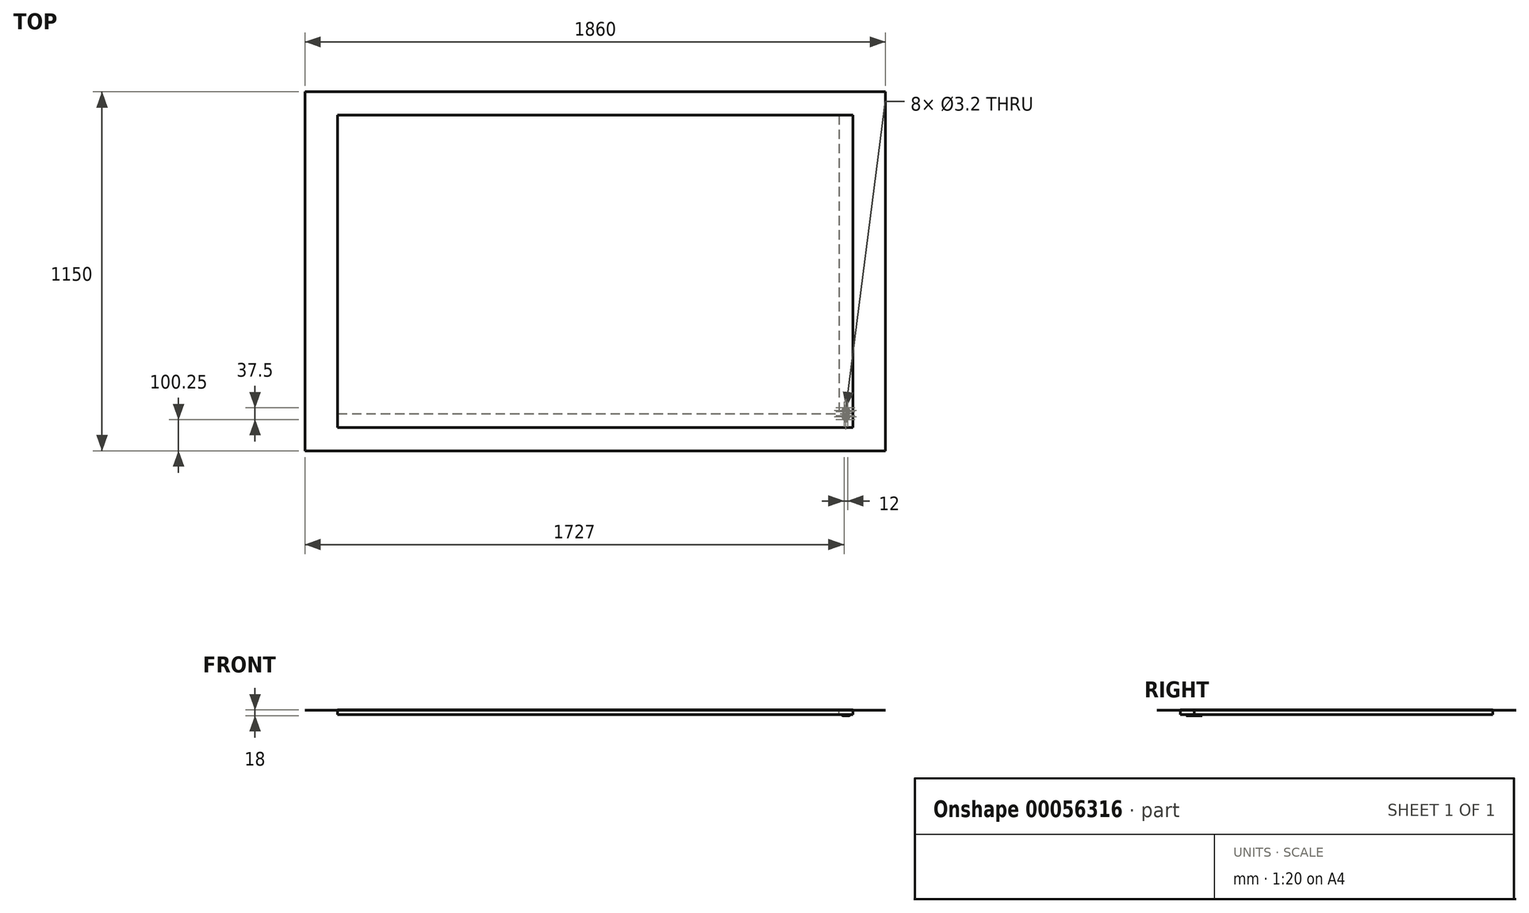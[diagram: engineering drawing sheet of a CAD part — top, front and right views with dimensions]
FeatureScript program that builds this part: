
annotation { "Feature Type Name" : "Feature", "Feature Type Description" : "" }
export const myFeature = defineFeature(function(context is Context, id is Id, definition is map)
    precondition{}
    {
        {
            var Q0;
            Q0=qCreatedBy(makeId("Top.planeOp"),FACE);
            var sketch = newSketch(context, id + "F0", { "sketchPlane" : qUnion([Q0])});
            skLineSegment(sketch, "E0.bottom", {"start": v(825, 500) * mm, "end": v(-825, 500) * mm});
            skLineSegment(sketch, "E0.top", {"start": v(825, -500) * mm, "end": v(-825, -500) * mm});
            skLineSegment(sketch, "E0.left", {"start": v(825, 500) * mm, "end": v(825, -500) * mm});
            skLineSegment(sketch, "E0.right", {"start": v(-825, 500) * mm, "end": v(-825, -500) * mm});
            skPoint(sketch, "E0.middle", {"position": v(0, 0) * mm});
            skSolve(sketch);
        }
        {
            var Q0;
            Q0 = qSketchRegion(id + "F0", true);
            extrude(context, id + "F1", {"entities" : qUnion([Q0]), "depth" : 1 * mm, "offsetDistance" : 25 * mm});
        }
        {
            var Q0;
            Q0=makeQuery(id+"F1.opExtrude","CAP_FACE",FACE,{"disambiguationData":[OSD([sQuery(id+"F0.wireOp",EDGE,"E0.bottom"),sQuery(id+"F0.wireOp",EDGE,"E0.top"),sQuery(id+"F0.wireOp",EDGE,"E0.left"),sQuery(id+"F0.wireOp",EDGE,"E0.right")])],"isStart":true});
            var sketch = newSketch(context, id + "F2", { "sketchPlane" : qUnion([Q0])});
            skLineSegment(sketch, "E1.bottom", {"start": v(930, -575) * mm, "end": v(-930, -575) * mm});
            skLineSegment(sketch, "E1.top", {"start": v(930, 575) * mm, "end": v(-930, 575) * mm});
            skLineSegment(sketch, "E1.left", {"start": v(930, -575) * mm, "end": v(930, 575) * mm});
            skLineSegment(sketch, "E1.right", {"start": v(-930, -575) * mm, "end": v(-930, 575) * mm});
            skPoint(sketch, "E1.middle", {"position": v(0, 0) * mm});
            skSolve(sketch);
        }
        {
            var Q0;
            Q0 = qSketchRegion(id + "F2", true);
            extrude(context, id + "F3", {"entities" : qUnion([Q0]), "depth" : 0.1 * mm, "offsetDistance" : 25 * mm});
        }
        {
            var Q0;
            Q0=makeQuery(id+"F1.opExtrude","CAP_FACE",FACE,{"disambiguationData":[OSD([sQuery(id+"F0.wireOp",EDGE,"E0.bottom"),sQuery(id+"F0.wireOp",EDGE,"E0.top"),sQuery(id+"F0.wireOp",EDGE,"E0.left"),sQuery(id+"F0.wireOp",EDGE,"E0.right")])],"isStart":true});
            var sketch = newSketch(context, id + "F4", { "sketchPlane" : qUnion([Q0])});
            skLineSegment(sketch, "E2.bottom", {"start": v(-825, 500) * mm, "end": v(825, 500) * mm});
            skLineSegment(sketch, "E2.top", {"start": v(-825, 456) * mm, "end": v(825, 456) * mm});
            skLineSegment(sketch, "E2.left", {"start": v(-825, 500) * mm, "end": v(-825, 456) * mm});
            skLineSegment(sketch, "E2.right", {"start": v(825, 500) * mm, "end": v(825, 456) * mm});
            skSolve(sketch);
        }
        {
            var Q0;
            Q0 = qSketchRegion(id + "F4", true);
            extrude(context, id + "F5", {"entities" : qUnion([Q0]), "depth" : 14 * mm, "offsetDistance" : 25 * mm});
        }
        {
            var Q0;
            Q0=makeQuery(id+"F1.opExtrude","CAP_FACE",FACE,{"disambiguationData":[OSD([sQuery(id+"F0.wireOp",EDGE,"E0.bottom"),sQuery(id+"F0.wireOp",EDGE,"E0.top"),sQuery(id+"F0.wireOp",EDGE,"E0.left"),sQuery(id+"F0.wireOp",EDGE,"E0.right")])],"isStart":true});
            var sketch = newSketch(context, id + "F6", { "sketchPlane" : qUnion([Q0])});
            skLineSegment(sketch, "E3.bottom", {"start": v(825, -500) * mm, "end": v(781, -500) * mm});
            skLineSegment(sketch, "E3.top", {"start": v(825, 456) * mm, "end": v(781, 456) * mm});
            skLineSegment(sketch, "E3.left", {"start": v(825, -500) * mm, "end": v(825, 456) * mm});
            skLineSegment(sketch, "E3.right", {"start": v(781, -500) * mm, "end": v(781, 456) * mm});
            skSolve(sketch);
        }
        {
            var Q0;
            Q0 = qSketchRegion(id + "F6", true);
            extrude(context, id + "F7", {"entities" : qUnion([Q0]), "depth" : 14 * mm, "offsetDistance" : 25 * mm});
        }
        {
            var Q0;
            Q0=makeQuery(id+"F5.opExtrude","CAP_FACE",FACE,{"disambiguationData":[OSD([sQuery(id+"F4.wireOp",EDGE,"E2.bottom"),sQuery(id+"F4.wireOp",EDGE,"E2.top"),sQuery(id+"F4.wireOp",EDGE,"E2.left"),sQuery(id+"F4.wireOp",EDGE,"E2.right")])],"isStart":false});
            var sketch = newSketch(context, id + "F8", { "sketchPlane" : qUnion([Q0])});
            skLineSegment(sketch, "E4.bottom", {"start": v(798, 456) * mm, "end": v(808, 456) * mm, "construction": true});
            skLineSegment(sketch, "E4.top", {"start": v(801, 431) * mm, "end": v(805, 431) * mm});
            skLineSegment(sketch, "E4.left", {"start": v(798, 456) * mm, "end": v(798, 434) * mm});
            skLineSegment(sketch, "E4.right", {"start": v(808, 456) * mm, "end": v(808, 434) * mm});
            skLineSegment(sketch, "E5", {"start": v(808, 431) * mm, "end": v(825, 431) * mm, "construction": true});
            skLineSegment(sketch, "E6", {"start": v(798, 431) * mm, "end": v(781, 431) * mm, "construction": true});
            skLineSegment(sketch, "E7", {"start": v(803, 431) * mm, "end": v(803, 456) * mm, "construction": true});
            skCircle(sketch, "E8", {"center": v(803, 437.25) * mm, "radius": 1.6 * mm});
            skLineSegment(sketch, "E9", {"start": v(808, 443.5) * mm, "end": v(798, 443.5) * mm, "construction": true});
            skCircle(sketch, "E10.MirrorC", {"center": v(803, 449.75) * mm, "radius": 1.6 * mm});
            skLineSegment(sketch, "E11", {"start": v(803, 443.5) * mm, "end": v(803, 431) * mm, "construction": true});
            skCircle(sketch, "E12.MirrorC", {"center": v(803, 474.75) * mm, "radius": 1.6 * mm});
            skCircle(sketch, "E13.MirrorC", {"center": v(803, 462.25) * mm, "radius": 1.6 * mm});
            skLineSegment(sketch, "E14.MirrorCS", {"start": v(801, 481) * mm, "end": v(805, 481) * mm});
            skLineSegment(sketch, "E15.MirrorCS", {"start": v(808, 456) * mm, "end": v(808, 478) * mm});
            skLineSegment(sketch, "E16.MirrorCS", {"start": v(798, 456) * mm, "end": v(798, 478) * mm});
            skPoint(sketch, "E17.visualSharp", {"position": v(798, 481) * mm});
            skArc(sketch, "E17.filletArc", {"start": v(801, 481) * mm, "mid": v(798.88, 480.12) * mm, "end": v(798, 478) * mm});
            skPoint(sketch, "E18.visualSharp", {"position": v(808, 481) * mm});
            skArc(sketch, "E18.filletArc", {"start": v(808, 478) * mm, "mid": v(807.12, 480.12) * mm, "end": v(805, 481) * mm});
            skPoint(sketch, "E19.visualSharp", {"position": v(808, 431) * mm});
            skArc(sketch, "E19.filletArc", {"start": v(805, 431) * mm, "mid": v(807.12, 431.88) * mm, "end": v(808, 434) * mm});
            skPoint(sketch, "E20.visualSharp", {"position": v(798, 431) * mm});
            skArc(sketch, "E20.filletArc", {"start": v(798, 434) * mm, "mid": v(798.88, 431.88) * mm, "end": v(801, 431) * mm});
            skSolve(sketch);
        }
        {
            var Q0;
            Q0 = qSketchRegion(id + "F8", true);
            extrude(context, id + "F9", {"entities" : qUnion([Q0]), "depth" : 3 * mm, "offsetDistance" : 25 * mm});
        }
        {
            var Q0;
            Q0=makeQuery(id+"F5.opExtrude","CAP_FACE",FACE,{"disambiguationData":[OSD([sQuery(id+"F4.wireOp",EDGE,"E2.bottom"),sQuery(id+"F4.wireOp",EDGE,"E2.top"),sQuery(id+"F4.wireOp",EDGE,"E2.left"),sQuery(id+"F4.wireOp",EDGE,"E2.right")])],"isStart":false});
            var sketch = newSketch(context, id + "F10", { "sketchPlane" : qUnion([Q0])});
            skLineSegment(sketch, "E21.bottom", {"start": v(794, 451) * mm, "end": v(798, 451) * mm});
            skLineSegment(sketch, "E21.top", {"start": v(794, 441) * mm, "end": v(812, 441) * mm});
            skLineSegment(sketch, "E21.left", {"start": v(791, 448) * mm, "end": v(791, 444) * mm});
            skLineSegment(sketch, "E21.right", {"start": v(815, 448) * mm, "end": v(815, 444) * mm});
            skLineSegment(sketch, "E22", {"start": v(791, 446) * mm, "end": v(781, 446) * mm, "construction": true});
            skLineSegment(sketch, "E23", {"start": v(815, 446) * mm, "end": v(825, 446) * mm, "construction": true});
            skLineSegment(sketch, "E24", {"start": v(791, 446) * mm, "end": v(803, 446) * mm, "construction": true});
            skPoint(sketch, "E24.endSnap0", {"position": v(803, 451) * mm});
            skLineSegment(sketch, "E25", {"start": v(803, 446) * mm, "end": v(803, 451) * mm, "construction": true});
            skCircle(sketch, "E26", {"center": v(797, 446) * mm, "radius": 1.6 * mm});
            skCircle(sketch, "E27.MirrorC", {"center": v(809, 446) * mm, "radius": 1.6 * mm});
            skLineSegment(sketch, "E28.top", {"start": v(798, 456) * mm, "end": v(808, 456) * mm});
            skLineSegment(sketch, "E28.left", {"start": v(798, 451) * mm, "end": v(798, 456) * mm});
            skLineSegment(sketch, "E28.right", {"start": v(808, 451) * mm, "end": v(808, 456) * mm});
            skLineSegment(sketch, "E29", {"start": v(803, 456) * mm, "end": v(803, 451) * mm, "construction": true});
            skLineSegment(sketch, "E30.trimOffspring", {"start": v(808, 451) * mm, "end": v(812, 451) * mm});
            skPoint(sketch, "E31.visualSharp", {"position": v(791, 451) * mm});
            skArc(sketch, "E31.filletArc", {"start": v(794, 451) * mm, "mid": v(791.88, 450.12) * mm, "end": v(791, 448) * mm});
            skPoint(sketch, "E32.visualSharp", {"position": v(791, 441) * mm});
            skArc(sketch, "E32.filletArc", {"start": v(791, 444) * mm, "mid": v(791.88, 441.88) * mm, "end": v(794, 441) * mm});
            skPoint(sketch, "E33.visualSharp", {"position": v(815, 441) * mm});
            skArc(sketch, "E33.filletArc", {"start": v(812, 441) * mm, "mid": v(814.12, 441.88) * mm, "end": v(815, 444) * mm});
            skPoint(sketch, "E34.visualSharp", {"position": v(815, 451) * mm});
            skArc(sketch, "E34.filletArc", {"start": v(815, 448) * mm, "mid": v(814.12, 450.12) * mm, "end": v(812, 451) * mm});
            skLineSegment(sketch, "E35", {"start": v(791, 451) * mm, "end": v(791, 441) * mm, "construction": true});
            skLineSegment(sketch, "E36.0", {"start": v(-825, 456) * mm, "end": v(825, 456) * mm, "construction": true});
            skLineSegment(sketch, "E37.MirrorCS", {"start": v(791, 464) * mm, "end": v(791, 468) * mm});
            skPoint(sketch, "E38.MirrorP", {"position": v(815, 471) * mm});
            skPoint(sketch, "E39.MirrorP", {"position": v(803, 461) * mm});
            skPoint(sketch, "E40.MirrorP", {"position": v(791, 471) * mm});
            skLineSegment(sketch, "E41.MirrorCS", {"start": v(808, 461) * mm, "end": v(808, 456) * mm});
            skLineSegment(sketch, "E42.MirrorCS", {"start": v(794, 471) * mm, "end": v(812, 471) * mm});
            skArc(sketch, "E43.MirrorCS", {"start": v(815, 464) * mm, "mid": v(814.12, 461.88) * mm, "end": v(812, 461) * mm});
            skLineSegment(sketch, "E44.MirrorCS", {"start": v(794, 461) * mm, "end": v(798, 461) * mm});
            skCircle(sketch, "E45.MirrorC", {"center": v(809, 466) * mm, "radius": 1.6 * mm});
            skArc(sketch, "E46.MirrorCS", {"start": v(794, 461) * mm, "mid": v(791.88, 461.88) * mm, "end": v(791, 464) * mm});
            skPoint(sketch, "E47.MirrorP", {"position": v(815, 461) * mm});
            skPoint(sketch, "E48.MirrorP", {"position": v(791, 461) * mm});
            skLineSegment(sketch, "E49.MirrorCS", {"start": v(815, 464) * mm, "end": v(815, 468) * mm});
            skLineSegment(sketch, "E50.MirrorCS", {"start": v(798, 461) * mm, "end": v(798, 456) * mm});
            skArc(sketch, "E51.MirrorCS", {"start": v(791, 468) * mm, "mid": v(791.88, 470.12) * mm, "end": v(794, 471) * mm});
            skArc(sketch, "E52.MirrorCS", {"start": v(812, 471) * mm, "mid": v(814.12, 470.12) * mm, "end": v(815, 468) * mm});
            skLineSegment(sketch, "E53.MirrorCS", {"start": v(808, 461) * mm, "end": v(812, 461) * mm});
            skCircle(sketch, "E54.MirrorC", {"center": v(797, 466) * mm, "radius": 1.6 * mm});
            skSolve(sketch);
        }
        {
            var Q0;
            Q0 = qSketchRegion(id + "F10", true);
            extrude(context, id + "F11", {"entities" : qUnion([Q0]), "depth" : 3 * mm, "offsetDistance" : 25 * mm});
        }
        {
            var Q0;
            Q0=makeQuery(id+"F11.opExtrude","SWEPT_EDGE",EDGE,{"disambiguationData":[OSD([sQuery(id+"F10.wireOp",EDGE,"E41.MirrorCS"),sQuery(id+"F10.wireOp",EDGE,"E53.MirrorCS")])]});
            var Q1;
            Q1=makeQuery(id+"F11.opExtrude","SWEPT_EDGE",EDGE,{"disambiguationData":[OSD([sQuery(id+"F10.wireOp",EDGE,"E28.right"),sQuery(id+"F10.wireOp",EDGE,"E30.trimOffspring")])]});
            var Q2;
            Q2=makeQuery(id+"F11.opExtrude","SWEPT_EDGE",EDGE,{"disambiguationData":[OSD([sQuery(id+"F10.wireOp",EDGE,"E44.MirrorCS"),sQuery(id+"F10.wireOp",EDGE,"E50.MirrorCS")])]});
            var Q3;
            Q3=makeQuery(id+"F11.opExtrude","SWEPT_EDGE",EDGE,{"disambiguationData":[OSD([sQuery(id+"F10.wireOp",EDGE,"E21.bottom"),sQuery(id+"F10.wireOp",EDGE,"E28.left")])]});
            fillet(context, id + "F12", {"entities" : qUnion([Q0, Q1, Q2, Q3]), "tangentPropagation" : true, "radius" : 5 * mm, "defaultsChanged" : false, "vertexSettings" : [], "allowEdgeOverflow" : false});
        }
        {
            var Q0;
            Q0=makeQuery(id+"F11.opExtrude","CAP_EDGE",EDGE,{"disambiguationData":[OSD([sQuery(id+"F10.wireOp",EDGE,"E27.MirrorC")])],"isStart":false});
            var Q1;
            Q1=makeQuery(id+"F11.opExtrude","CAP_EDGE",EDGE,{"disambiguationData":[OSD([sQuery(id+"F10.wireOp",EDGE,"E26")])],"isStart":false});
            var Q2;
            Q2=makeQuery(id+"F11.opExtrude","CAP_EDGE",EDGE,{"disambiguationData":[OSD([sQuery(id+"F10.wireOp",EDGE,"E45.MirrorC")])],"isStart":false});
            var Q3;
            Q3=makeQuery(id+"F11.opExtrude","CAP_EDGE",EDGE,{"disambiguationData":[OSD([sQuery(id+"F10.wireOp",EDGE,"E54.MirrorC")])],"isStart":false});
            chamfer(context, id + "F13", {"entities" : qUnion([Q0, Q1, Q2, Q3]), "chamferType" : ChamferType.TWO_OFFSETS, "width1" : 1.7 * mm, "oppositeDirection" : false, "width2" : 1 * mm, "tangentPropagation" : true});
        }
        {
            var Q0;
            Q0=makeQuery(id+"F11.opExtrude","CAP_EDGE",EDGE,{"disambiguationData":[OSD([sQuery(id+"F10.wireOp",EDGE,"E33.filletArc")])],"isStart":false});
            chamfer(context, id + "F14", {"entities" : qUnion([Q0]), "width" : 1 * mm, "tangentPropagation" : true});
        }
    });
